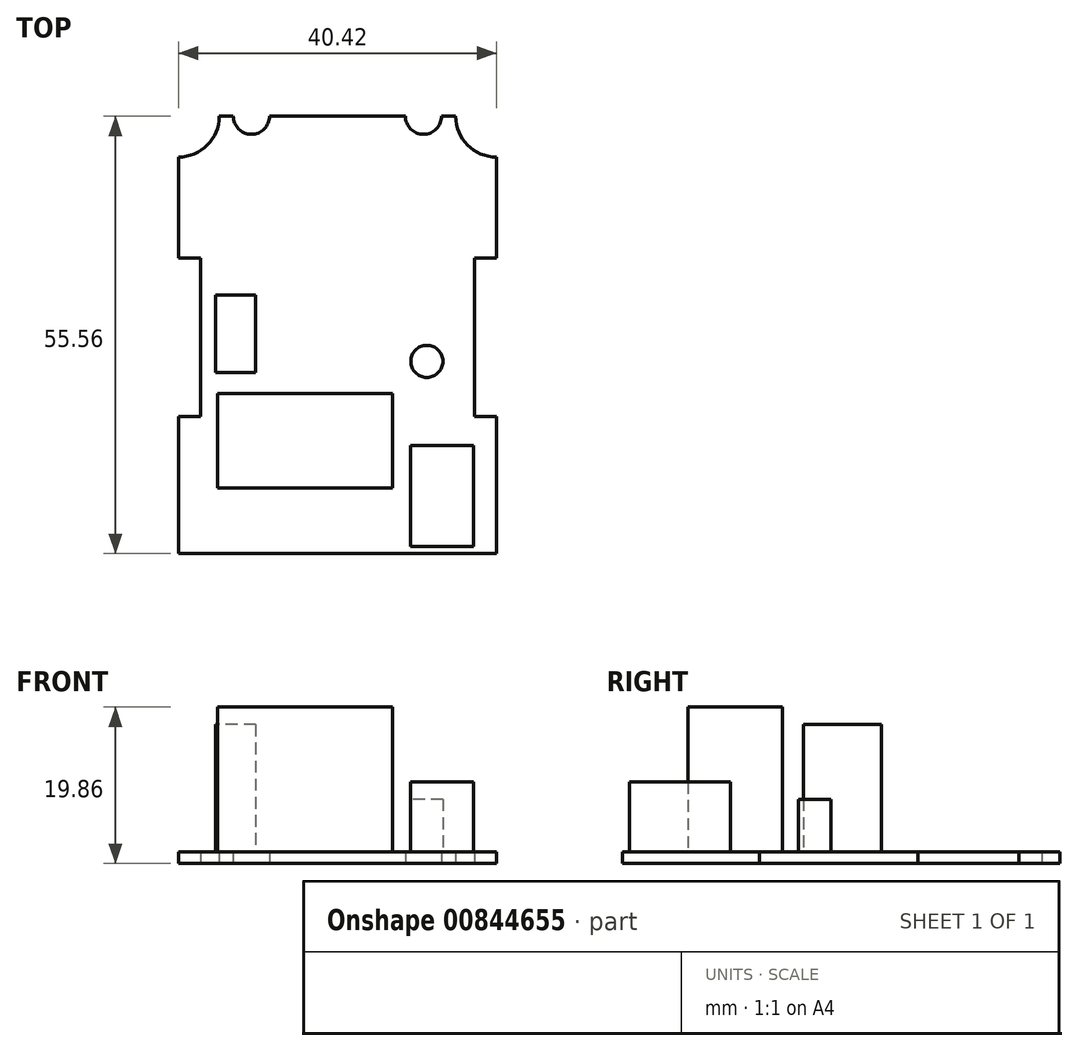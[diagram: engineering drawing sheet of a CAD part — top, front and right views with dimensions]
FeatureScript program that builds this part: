
annotation { "Feature Type Name" : "Feature", "Feature Type Description" : "" }
export const myFeature = defineFeature(function(context is Context, id is Id, definition is map)
    precondition{}
    {
        {
            var Q0;
            Q0=qCreatedBy(makeId("Top.planeOp"),FACE);
            var sketch = newSketch(context, id + "F0", { "sketchPlane" : qUnion([Q0])});
            skLineSegment(sketch, "E0.bottom", {"start": v(20.21, -27.78) * mm, "end": v(-20.21, -27.78) * mm});
            skLineSegment(sketch, "E0.top", {"start": v(15.01, 27.78) * mm, "end": v(13.23, 27.78) * mm});
            skLineSegment(sketch, "E0.left", {"start": v(20.21, -27.78) * mm, "end": v(20.21, -10.35) * mm});
            skLineSegment(sketch, "E0.right", {"start": v(-20.21, -27.78) * mm, "end": v(-20.21, -10.36) * mm});
            skPoint(sketch, "E0.middle", {"position": v(0, 0) * mm});
            skArc(sketch, "E1", {"start": v(-15.01, 27.77) * mm, "mid": v(-16.53, 24.1) * mm, "end": v(-20.21, 22.58) * mm});
            skArc(sketch, "E2", {"start": v(15.01, 27.77) * mm, "mid": v(16.53, 24.1) * mm, "end": v(20.21, 22.58) * mm});
            skArc(sketch, "E3", {"start": v(-13.23, 27.77) * mm, "mid": v(-10.93, 25.47) * mm, "end": v(-8.63, 27.77) * mm});
            skArc(sketch, "E4", {"start": v(8.63, 27.77) * mm, "mid": v(10.93, 25.47) * mm, "end": v(13.23, 27.77) * mm});
            skLineSegment(sketch, "E5.trimOffspring", {"start": v(-13.23, 27.78) * mm, "end": v(-15.01, 27.78) * mm});
            skLineSegment(sketch, "E6.trimOffspring", {"start": v(8.63, 27.78) * mm, "end": v(-8.63, 27.78) * mm});
            skLineSegment(sketch, "E7.bottom", {"start": v(20.21, 9.78) * mm, "end": v(17.41, 9.78) * mm});
            skLineSegment(sketch, "E7.top", {"start": v(20.21, -10.36) * mm, "end": v(17.41, -10.36) * mm});
            skLineSegment(sketch, "E7.right", {"start": v(17.41, 9.78) * mm, "end": v(17.41, -10.36) * mm});
            skLineSegment(sketch, "E8.MirrorCS", {"start": v(-17.41, 9.78) * mm, "end": v(-17.41, -10.36) * mm});
            skLineSegment(sketch, "E9.MirrorCS", {"start": v(-20.21, 9.78) * mm, "end": v(-17.41, 9.78) * mm});
            skLineSegment(sketch, "E10.MirrorCS", {"start": v(-20.21, -10.36) * mm, "end": v(-17.41, -10.36) * mm});
            skLineSegment(sketch, "E11.trimOffspring", {"start": v(-20.21, 9.78) * mm, "end": v(-20.21, 22.57) * mm});
            skLineSegment(sketch, "E12.trimOffspring", {"start": v(20.21, 9.78) * mm, "end": v(20.21, 22.58) * mm});
            skSolve(sketch);
        }
        {
            var Q0;
            Q0=makeQuery(id+"F0.imprint","IMPRINT",FACE,{"disambiguationData":[TD([[makeQuery(id+"F0.imprint","IMPRINT",EDGE,{"derivedFrom":sQuery(id+"F0.wireOp",EDGE,"E0.bottom")}),-1.0]])]});
            extrude(context, id + "F1", {"entities" : qUnion([Q0]), "depth" : 1.44 * mm, "offsetDistance" : 25 * mm});
        }
        {
            var Q0;
            Q0=makeQuery(id+"F1.opExtrude","CAP_FACE",FACE,{"disambiguationData":[OSD([sQuery(id+"F0.wireOp",EDGE,"E0.bottom"),sQuery(id+"F0.wireOp",EDGE,"E0.top"),sQuery(id+"F0.wireOp",EDGE,"E0.left"),sQuery(id+"F0.wireOp",EDGE,"E0.right"),sQuery(id+"F0.wireOp",EDGE,"E1"),sQuery(id+"F0.wireOp",EDGE,"E2"),sQuery(id+"F0.wireOp",EDGE,"E3"),sQuery(id+"F0.wireOp",EDGE,"E4"),sQuery(id+"F0.wireOp",EDGE,"E5.trimOffspring"),sQuery(id+"F0.wireOp",EDGE,"E6.trimOffspring"),sQuery(id+"F0.wireOp",EDGE,"E7.bottom"),sQuery(id+"F0.wireOp",EDGE,"E7.top"),sQuery(id+"F0.wireOp",EDGE,"E7.right"),sQuery(id+"F0.wireOp",EDGE,"E8.MirrorCS"),sQuery(id+"F0.wireOp",EDGE,"E9.MirrorCS"),sQuery(id+"F0.wireOp",EDGE,"E10.MirrorCS"),sQuery(id+"F0.wireOp",EDGE,"E11.trimOffspring"),sQuery(id+"F0.wireOp",EDGE,"E12.trimOffspring")])],"isStart":false});
            var sketch = newSketch(context, id + "F2", { "sketchPlane" : qUnion([Q0])});
            skLineSegment(sketch, "E13.bottom", {"start": v(-15.21, -7.48) * mm, "end": v(6.99, -7.48) * mm});
            skLineSegment(sketch, "E13.top", {"start": v(-15.21, -19.48) * mm, "end": v(6.99, -19.48) * mm});
            skLineSegment(sketch, "E13.left", {"start": v(-15.21, -7.48) * mm, "end": v(-15.21, -19.48) * mm});
            skLineSegment(sketch, "E13.right", {"start": v(7, -7.48) * mm, "end": v(7, -19.48) * mm});
            skLineSegment(sketch, "E14.bottom", {"start": v(9.31, -26.88) * mm, "end": v(17.31, -26.88) * mm});
            skLineSegment(sketch, "E14.top", {"start": v(9.3, -14.08) * mm, "end": v(17.3, -14.08) * mm});
            skLineSegment(sketch, "E14.left", {"start": v(9.31, -26.88) * mm, "end": v(9.3, -14.08) * mm});
            skLineSegment(sketch, "E14.right", {"start": v(17.31, -26.88) * mm, "end": v(17.31, -14.08) * mm});
            skCircle(sketch, "E15", {"center": v(11.36, -3.37) * mm, "radius": 2.04 * mm});
            skLineSegment(sketch, "E16.bottom", {"start": v(-10.38, -4.82) * mm, "end": v(-15.48, -4.82) * mm});
            skLineSegment(sketch, "E16.top", {"start": v(-10.38, 5.08) * mm, "end": v(-15.48, 5.08) * mm});
            skLineSegment(sketch, "E16.left", {"start": v(-10.38, -4.82) * mm, "end": v(-10.38, 5.08) * mm});
            skLineSegment(sketch, "E16.right", {"start": v(-15.48, -4.82) * mm, "end": v(-15.48, 5.08) * mm});
            skSolve(sketch);
        }
        {
            var Q0;
            Q0=makeQuery(id+"F2.imprint","IMPRINT",FACE,{"disambiguationData":[TD([[makeQuery(id+"F2.imprint","IMPRINT",EDGE,{"derivedFrom":sQuery(id+"F2.wireOp",EDGE,"E13.bottom")}),-1.0]])]});
            extrude(context, id + "F3", {"entities" : qUnion([Q0]), "operationType" : NewBodyOperationType.ADD, "depth" : 18.42 * mm, "offsetDistance" : 25 * mm});
        }
        {
            var Q0;
            Q0=makeQuery(id+"F2.imprint","IMPRINT",FACE,{"disambiguationData":[TD([[makeQuery(id+"F2.imprint","IMPRINT",EDGE,{"derivedFrom":sQuery(id+"F2.wireOp",EDGE,"E16.bottom")}),-1.0]])]});
            extrude(context, id + "F4", {"entities" : qUnion([Q0]), "operationType" : NewBodyOperationType.ADD, "depth" : 16.2 * mm, "offsetDistance" : 25 * mm});
        }
        {
            var Q0;
            Q0=makeQuery(id+"F2.imprint","IMPRINT",FACE,{"disambiguationData":[TD([[makeQuery(id+"F2.imprint","IMPRINT",EDGE,{"derivedFrom":sQuery(id+"F2.wireOp",EDGE,"E14.bottom")}),1.0]])]});
            extrude(context, id + "F5", {"entities" : qUnion([Q0]), "operationType" : NewBodyOperationType.ADD, "depth" : 8.9 * mm, "offsetDistance" : 25 * mm});
        }
        {
            var Q0;
            Q0=makeQuery(id+"F2.imprint","IMPRINT",FACE,{"disambiguationData":[TD([[makeQuery(id+"F2.imprint","IMPRINT",EDGE,{"derivedFrom":sQuery(id+"F2.wireOp",EDGE,"E15")}),1.0]])]});
            extrude(context, id + "F6", {"entities" : qUnion([Q0]), "operationType" : NewBodyOperationType.ADD, "depth" : 6.7 * mm, "offsetDistance" : 25 * mm});
        }
    });
